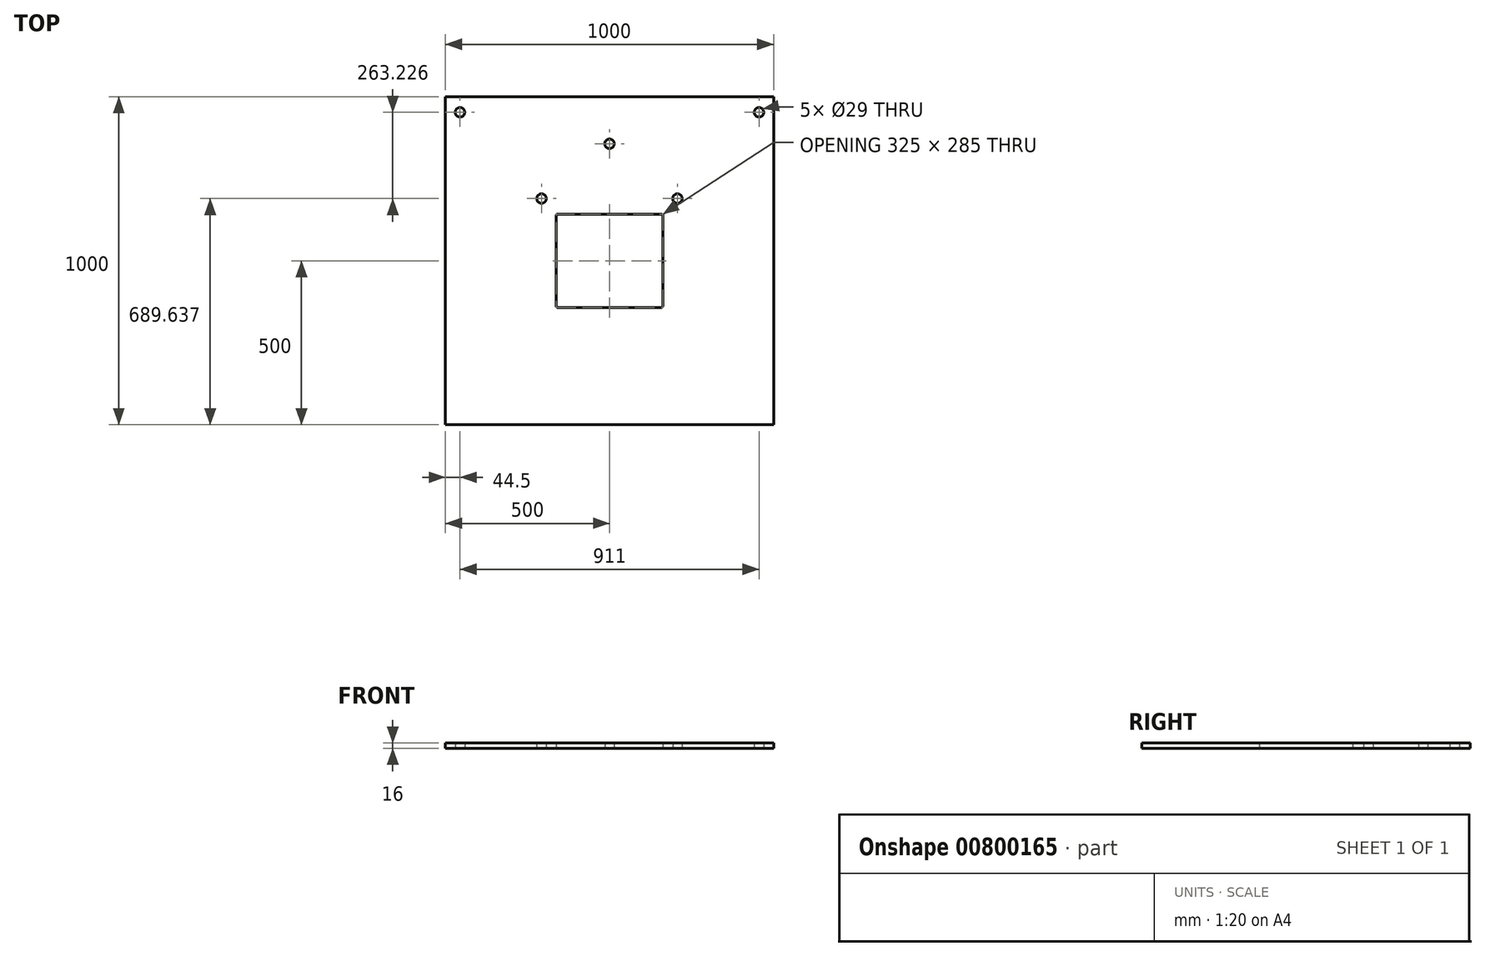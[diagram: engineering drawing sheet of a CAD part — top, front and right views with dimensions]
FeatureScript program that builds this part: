
annotation { "Feature Type Name" : "Feature", "Feature Type Description" : "" }
export const myFeature = defineFeature(function(context is Context, id is Id, definition is map)
    precondition{}
    {
        {
            var Q0;
            Q0=qCreatedBy(makeId("Top.planeOp"),FACE);
            var sketch = newSketch(context, id + "F0", { "sketchPlane" : qUnion([Q0])});
            skLineSegment(sketch, "E0.bottom", {"start": v(0, 0) * mm, "end": v(1000, 0) * mm});
            skLineSegment(sketch, "E0.top", {"start": v(0, 1000) * mm, "end": v(1000, 1000) * mm});
            skLineSegment(sketch, "E0.left", {"start": v(0, 0) * mm, "end": v(0, 1000) * mm});
            skLineSegment(sketch, "E0.right", {"start": v(1000, 0) * mm, "end": v(1000, 1000) * mm});
            skLineSegment(sketch, "E1", {"start": v(500, 1000) * mm, "end": v(500, 0) * mm, "construction": true});
            skLineSegment(sketch, "E2", {"start": v(0, 500) * mm, "end": v(1000, 500) * mm, "construction": true});
            skLineSegment(sketch, "E3.bottom", {"start": v(657.5, 642.5) * mm, "end": v(342.5, 642.5) * mm});
            skLineSegment(sketch, "E3.top", {"start": v(657.5, 357.5) * mm, "end": v(342.5, 357.5) * mm});
            skLineSegment(sketch, "E3.left", {"start": v(662.5, 637.5) * mm, "end": v(662.5, 362.5) * mm});
            skLineSegment(sketch, "E3.right", {"start": v(337.5, 637.5) * mm, "end": v(337.5, 362.5) * mm});
            skPoint(sketch, "E3.middle", {"position": v(500, 500) * mm});
            skPoint(sketch, "E4.visualSharp", {"position": v(337.5, 642.5) * mm});
            skArc(sketch, "E4.filletArc", {"start": v(342.5, 642.5) * mm, "mid": v(338.96, 641.04) * mm, "end": v(337.5, 637.5) * mm});
            skPoint(sketch, "E5.visualSharp", {"position": v(662.5, 642.5) * mm});
            skArc(sketch, "E5.filletArc", {"start": v(662.5, 637.5) * mm, "mid": v(661.04, 641.04) * mm, "end": v(657.5, 642.5) * mm});
            skPoint(sketch, "E6.visualSharp", {"position": v(337.5, 357.5) * mm});
            skArc(sketch, "E6.filletArc", {"start": v(337.5, 362.5) * mm, "mid": v(338.96, 358.96) * mm, "end": v(342.5, 357.5) * mm});
            skPoint(sketch, "E7.visualSharp", {"position": v(662.5, 357.5) * mm});
            skArc(sketch, "E7.filletArc", {"start": v(657.5, 357.5) * mm, "mid": v(661.04, 358.96) * mm, "end": v(662.5, 362.5) * mm});
            skCircle(sketch, "E8", {"center": v(707, 689.64) * mm, "radius": 14.5 * mm});
            skLineSegment(sketch, "E9", {"start": v(662.5, 642.5) * mm, "end": v(1000, 1000) * mm, "construction": true});
            skCircle(sketch, "E10", {"center": v(955.5, 952.86) * mm, "radius": 14.5 * mm});
            skLineSegment(sketch, "E11", {"start": v(0, 1000) * mm, "end": v(337.5, 642.5) * mm, "construction": true});
            skCircle(sketch, "E12", {"center": v(500, 856.72) * mm, "radius": 14.5 * mm});
            skCircle(sketch, "E13", {"center": v(293, 689.64) * mm, "radius": 14.5 * mm});
            skCircle(sketch, "E14", {"center": v(44.5, 952.86) * mm, "radius": 14.5 * mm});
            skLineSegment(sketch, "E15", {"start": v(44.5, 952.86) * mm, "end": v(955.5, 952.86) * mm, "construction": true});
            skLineSegment(sketch, "E16", {"start": v(293, 689.64) * mm, "end": v(707, 689.64) * mm, "construction": true});
            skSolve(sketch);
        }
        {
            var Q0;
            Q0=makeQuery(id+"F0.imprint","IMPRINT",FACE,{"disambiguationData":[TD([[makeQuery(id+"F0.imprint","IMPRINT",EDGE,{"derivedFrom":sQuery(id+"F0.wireOp",EDGE,"E0.bottom")}),1.0]])]});
            extrude(context, id + "F1", {"entities" : qUnion([Q0]), "depth" : 16 * mm, "offsetDistance" : 25 * mm});
        }
    });
